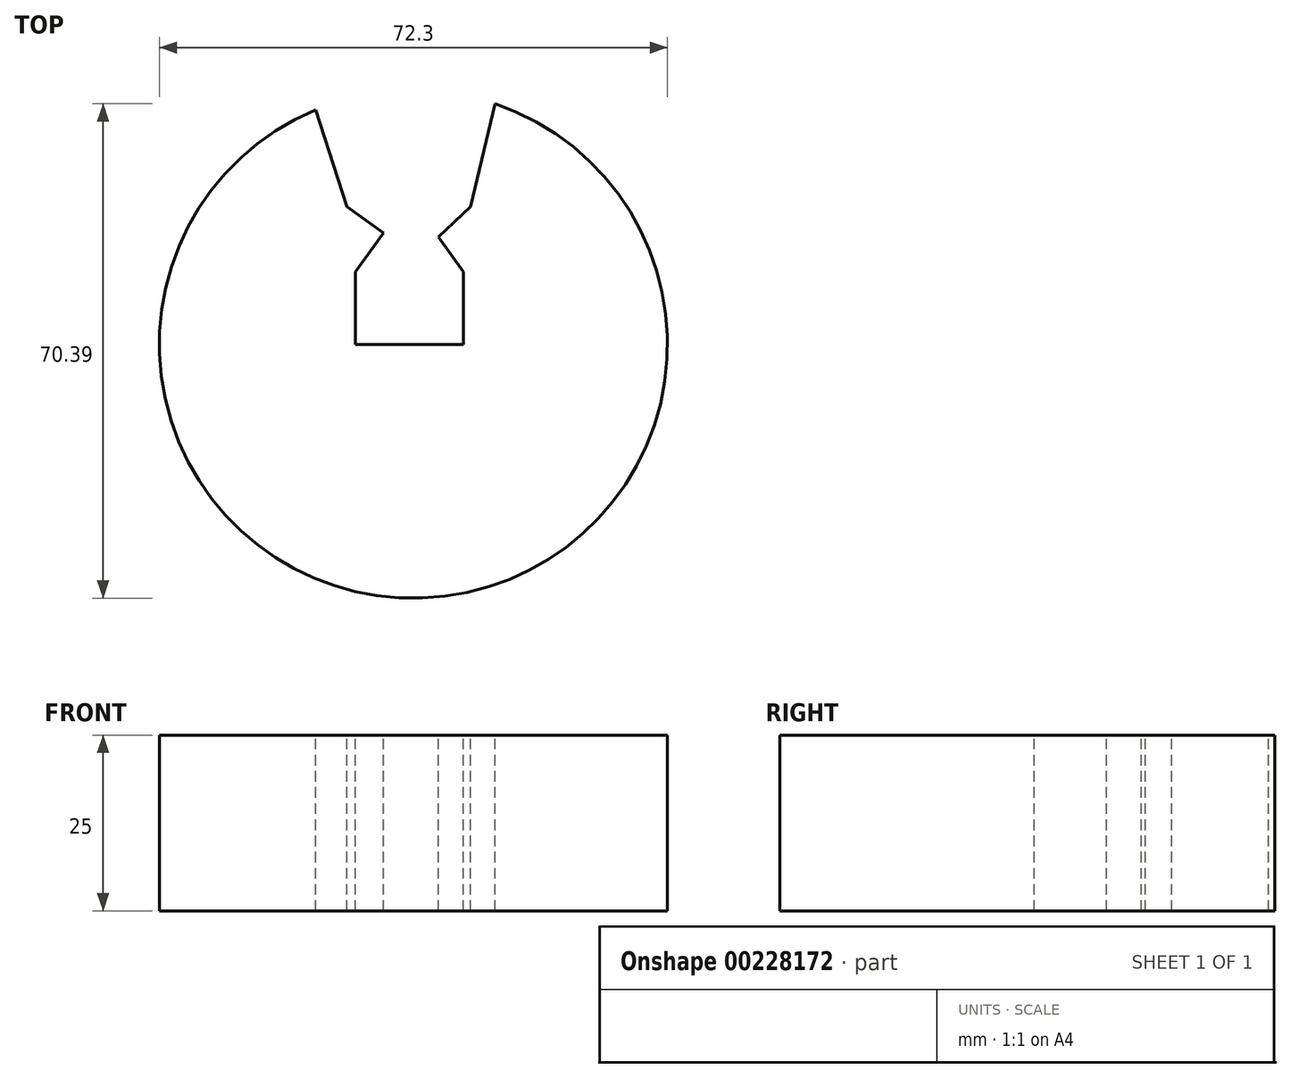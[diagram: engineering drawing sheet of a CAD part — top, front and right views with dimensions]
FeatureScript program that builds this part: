
annotation { "Feature Type Name" : "Feature", "Feature Type Description" : "" }
export const myFeature = defineFeature(function(context is Context, id is Id, definition is map)
    precondition{}
    {
        {
            var Q0;
            Q0=qCreatedBy(makeId("Top.planeOp"),FACE);
            var sketch = newSketch(context, id + "F0", { "sketchPlane" : qUnion([Q0])});
            skCircle(sketch, "E0", {"center": v(0, 0) * mm, "radius": 36.15 * mm});
            skSolve(sketch);
        }
        {
            var Q0;
            Q0=makeQuery(id+"F0.imprint","IMPRINT",FACE,{"disambiguationData":[TD([[makeQuery(id+"F0.imprint","IMPRINT",EDGE,{"derivedFrom":sQuery(id+"F0.wireOp",EDGE,"E0")}),1.0]])]});
            extrude(context, id + "F1", {"entities" : qUnion([Q0]), "depth" : 25 * mm});
        }
        {
            var Q0;
            Q0=makeQuery(id+"F1.opExtrude","CAP_FACE",FACE,{"disambiguationData":[OSD([sQuery(id+"F0.wireOp",EDGE,"E0")])],"isStart":false});
            var sketch = newSketch(context, id + "F2", { "sketchPlane" : qUnion([Q0])});
            skLineSegment(sketch, "E1", {"start": v(0, 0) * mm, "end": v(0, 36.15) * mm});
            skLineSegment(sketch, "E2", {"start": v(0, 0) * mm, "end": v(0, -36.15) * mm});
            skLineSegment(sketch, "E3", {"start": v(0, 0) * mm, "end": v(-36.15, 0) * mm});
            skLineSegment(sketch, "E4", {"start": v(0, 0) * mm, "end": v(36.15, 0) * mm});
            skLineSegment(sketch, "E5", {"start": v(-13.92, 33.36) * mm, "end": v(-8.24, 15.83) * mm});
            skLineSegment(sketch, "E6", {"start": v(11.6, 34.24) * mm, "end": v(7.13, 15.27) * mm});
            skLineSegment(sketch, "E7", {"start": v(7.13, 15.27) * mm, "end": v(7.13, 0) * mm});
            skLineSegment(sketch, "E8", {"start": v(-8.24, 15.83) * mm, "end": v(-8.24, 0) * mm});
            skLineSegment(sketch, "E9", {"start": v(-4.27, 15.83) * mm, "end": v(-8.24, 10.33) * mm});
            skLineSegment(sketch, "E10", {"start": v(-8.24, 10.33) * mm, "end": v(-4.27, 15.83) * mm});
            skLineSegment(sketch, "E11", {"start": v(-4.27, 15.83) * mm, "end": v(-9.45, 19.56) * mm});
            skLineSegment(sketch, "E12", {"start": v(8.14, 19.56) * mm, "end": v(3.53, 15.27) * mm});
            skLineSegment(sketch, "E13", {"start": v(3.53, 15.27) * mm, "end": v(7.13, 10.33) * mm});
            skSolve(sketch);
        }
        {
            var Q0;
            {var subQ8=sQuery(id+"F2.wireOp",EDGE,"E1");Q0=makeQuery(id+"F2.imprint","IMPRINT",FACE,{"disambiguationData":[TD([[makeQuery(id+"F2.imprint","IMPRINT",EDGE,{"derivedFrom":subQ8}),1.0]])]});}
            var Q1;
            {var subQ1=sQuery(id+"F2.wireOp",EDGE,"E1");Q1=makeQuery(id+"F2.imprint","IMPRINT",FACE,{"disambiguationData":[TD([[makeQuery(id+"F2.imprint","IMPRINT",EDGE,{"derivedFrom":subQ1}),-1.0]])]});}
            extrude(context, id + "F3", {"entities" : qUnion([Q0, Q1]), "operationType" : NewBodyOperationType.REMOVE, "oppositeDirection" : true, "depth" : 25 * mm});
        }
    });
